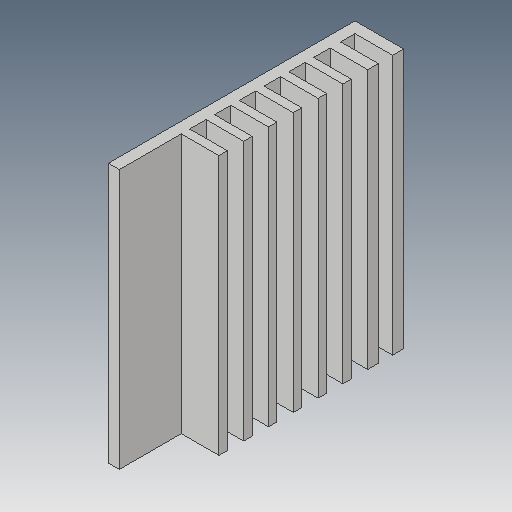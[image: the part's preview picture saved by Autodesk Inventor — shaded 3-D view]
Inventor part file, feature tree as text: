
AUTODESK INVENTOR PART (.ipt)
format: ipt  version: 2018 (Build 220112000, 112)  size: 188,928 bytes
history: native  units: mm
features: extrude x7, sketch x7, projected_geometry x5, mirror x1, pattern_linear x1
ambient origin geometry x8: Origin, YZ Plane, XZ Plane, XY Plane, X Axis, Y Axis, Z Axis, Center Point
bodies: Solid1 (feature_tree)
feature tree (21):
  extrude  "Extrusion1"  Depth=40.0mm
  extrude  "Extrusion2"  Depth=1.7mm
  mirror  "Mirror1"
  extrude  "Extrusion3"  Depth=2.2mm
  pattern_linear  "Rectangular Pattern1"  Count1=8 Spacing1=3.82mm
  extrude  "Extrusion4"  Depth=3.82mm TaperAngle=0.0deg
  extrude  "Extrusion5"  Depth=3.82mm TaperAngle=0.0deg
  extrude  "Extrusion8"  Depth=3.82mm TaperAngle=0.0deg
  extrude  "Extrusion9"  Depth=3.82mm TaperAngle=0.0deg
  sketch  "Sketch1"  dims[d0=20.0mm d1=40.0mm]
  sketch  "Sketch2"  dims[d2=40.0mm d3=0.0mm d4=1.7mm]
  projected_geometry  "Projected Loop1"
  sketch  "Sketch3"  dims[d5=4.2mm d6=2.2mm]
  projected_geometry  "Projected Loop2"
  sketch  "Sketch4"  dims[d7=85.0mm d8=0.0mm]
  projected_geometry  "Projected Loop3"
  sketch  "Sketch5"  dims[d9=1.3mm]
  sketch  "Sketch8"  dims[d10=2.52mm]
  projected_geometry  "Projected Loop5"
  sketch  "Sketch9"  dims[d11=85.0mm d12=0.0mm d13=80.0mm d15=3.82mm d16=2.5mm d17=0.0mm d18=10.0mm d19=0.0mm d32=10.0mm d33=0.0mm d34=2.0mm d35=0.0mm]
  projected_geometry  "Projected Loop6"
